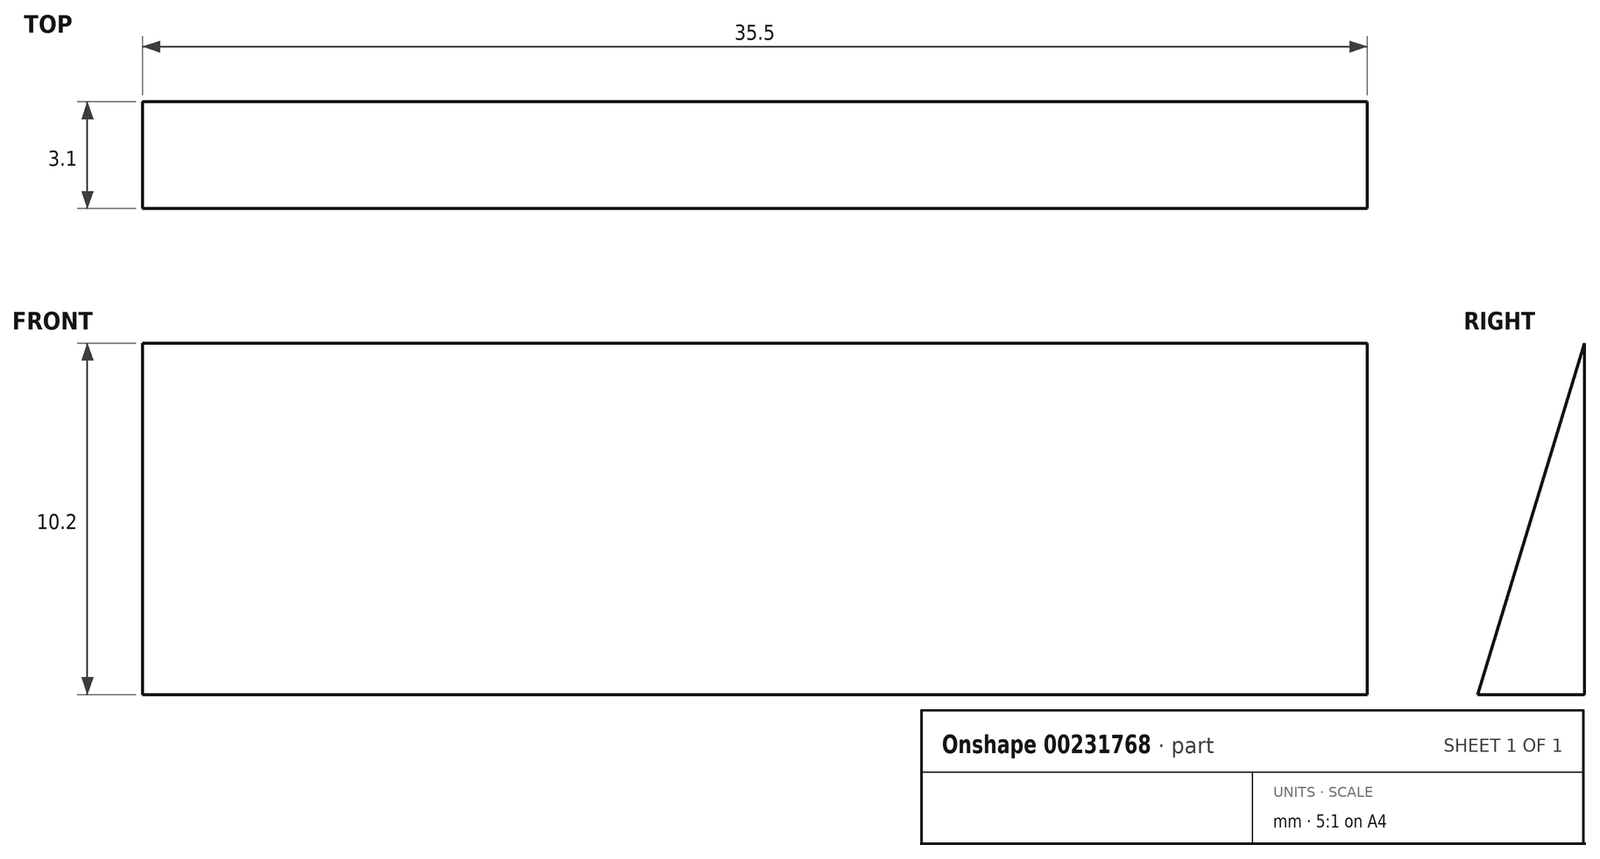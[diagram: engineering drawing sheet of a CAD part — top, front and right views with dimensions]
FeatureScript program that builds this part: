
annotation { "Feature Type Name" : "Feature", "Feature Type Description" : "" }
export const myFeature = defineFeature(function(context is Context, id is Id, definition is map)
    precondition{}
    {
        {
            var Q0;
            Q0=qCreatedBy(makeId("Right.planeOp"),FACE);
            var sketch = newSketch(context, id + "F0", { "sketchPlane" : qUnion([Q0])});
            skLineSegment(sketch, "E0", {"start": v(0, 0) * mm, "end": v(3.1, 10.2) * mm});
            skLineSegment(sketch, "E1", {"start": v(3.1, 10.2) * mm, "end": v(3.1, 0) * mm});
            skLineSegment(sketch, "E2", {"start": v(3.1, 0) * mm, "end": v(0, 0) * mm});
            skSolve(sketch);
        }
        {
            var Q0;
            Q0 = qSketchRegion(id + "F0", true);
            extrude(context, id + "F1", {"entities" : qUnion([Q0]), "depth" : 35.5 * mm});
        }
    });
